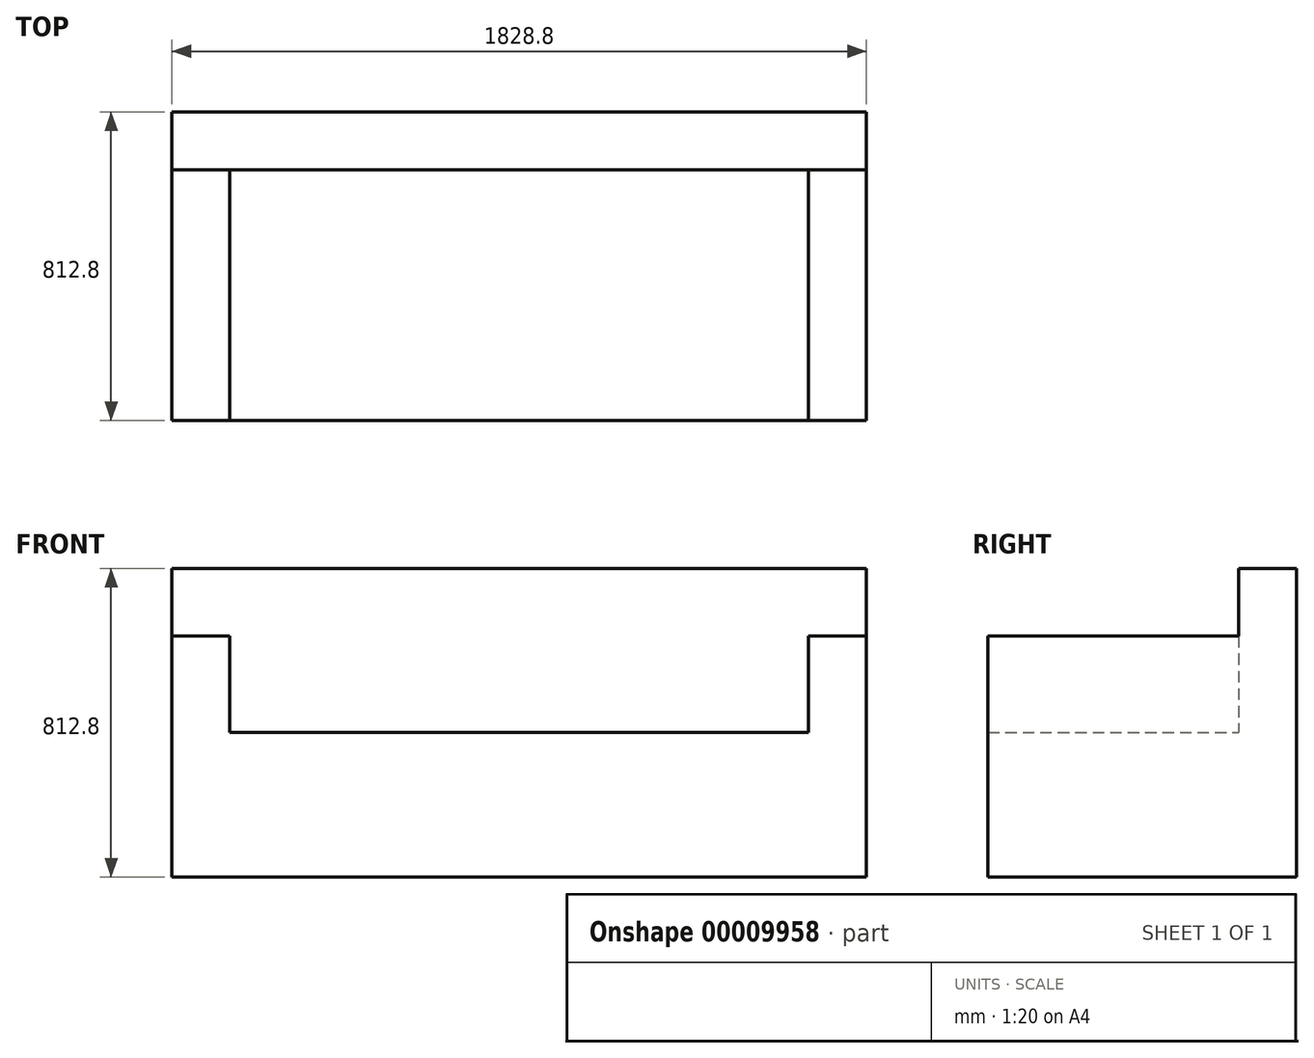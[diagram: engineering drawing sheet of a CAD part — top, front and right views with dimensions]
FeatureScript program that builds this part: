
annotation { "Feature Type Name" : "Feature", "Feature Type Description" : "" }
export const myFeature = defineFeature(function(context is Context, id is Id, definition is map)
    precondition{}
    {
        {
            var Q0;
            Q0=qCreatedBy(makeId("Top.planeOp"),FACE);
            var sketch = newSketch(context, id + "F0", { "sketchPlane" : qUnion([Q0])});
            skLineSegment(sketch, "E0.bottom", {"start": v(0, 0) * mm, "end": v(1828.8, 0) * mm});
            skLineSegment(sketch, "E0.top", {"start": v(0, -812.8) * mm, "end": v(1828.8, -812.8) * mm});
            skLineSegment(sketch, "E0.left", {"start": v(0, 0) * mm, "end": v(0, -812.8) * mm});
            skLineSegment(sketch, "E0.right", {"start": v(1828.8, 0) * mm, "end": v(1828.8, -812.8) * mm});
            skSolve(sketch);
        }
        {
            var Q0;
            Q0 = qSketchRegion(id + "F0", true);
            extrude(context, id + "F1", {"entities" : qUnion([Q0]), "depth" : 381 * mm});
        }
        {
            var Q0;
            Q0=makeQuery(id+"F1.opExtrude","CAP_FACE",FACE,{"disambiguationData":[OSD([sQuery(id+"F0.wireOp",EDGE,"E0.bottom"),sQuery(id+"F0.wireOp",EDGE,"E0.top"),sQuery(id+"F0.wireOp",EDGE,"E0.left"),sQuery(id+"F0.wireOp",EDGE,"E0.right")])],"isStart":false});
            var sketch = newSketch(context, id + "F2", { "sketchPlane" : qUnion([Q0])});
            skLineSegment(sketch, "E1", {"start": v(0, -812.8) * mm, "end": v(0, 0) * mm});
            skLineSegment(sketch, "E2", {"start": v(0, 0) * mm, "end": v(1828.8, 0) * mm});
            skLineSegment(sketch, "E3", {"start": v(1828.8, 0) * mm, "end": v(1828.8, -812.8) * mm});
            skLineSegment(sketch, "E4", {"start": v(1828.8, -812.8) * mm, "end": v(1676.4, -812.8) * mm});
            skLineSegment(sketch, "E5", {"start": v(1676.4, -812.8) * mm, "end": v(1676.4, -152.4) * mm});
            skLineSegment(sketch, "E6", {"start": v(1676.4, -152.4) * mm, "end": v(152.4, -152.4) * mm});
            skLineSegment(sketch, "E7", {"start": v(152.4, -152.4) * mm, "end": v(152.4, -812.8) * mm});
            skLineSegment(sketch, "E8", {"start": v(152.4, -812.8) * mm, "end": v(0, -812.8) * mm});
            skSolve(sketch);
        }
        {
            var Q0;
            Q0 = qSketchRegion(id + "F2", true);
            extrude(context, id + "F3", {"entities" : qUnion([Q0]), "operationType" : NewBodyOperationType.ADD, "depth" : 254 * mm});
        }
        {
            var Q0;
            Q0=makeQuery(id+"F3.opExtrude","CAP_FACE",FACE,{"disambiguationData":[OSD([sQuery(id+"F2.wireOp",EDGE,"E1"),sQuery(id+"F2.wireOp",EDGE,"E2"),sQuery(id+"F2.wireOp",EDGE,"E3"),sQuery(id+"F2.wireOp",EDGE,"E4"),sQuery(id+"F2.wireOp",EDGE,"E5"),sQuery(id+"F2.wireOp",EDGE,"E6"),sQuery(id+"F2.wireOp",EDGE,"E7"),sQuery(id+"F2.wireOp",EDGE,"E8")])],"isStart":false});
            var sketch = newSketch(context, id + "F4", { "sketchPlane" : qUnion([Q0])});
            skLineSegment(sketch, "E9.bottom", {"start": v(0, 0) * mm, "end": v(1828.8, 0) * mm});
            skLineSegment(sketch, "E9.top", {"start": v(0, -152.4) * mm, "end": v(1828.8, -152.4) * mm});
            skLineSegment(sketch, "E9.left", {"start": v(0, 0) * mm, "end": v(0, -152.4) * mm});
            skLineSegment(sketch, "E9.right", {"start": v(1828.8, 0) * mm, "end": v(1828.8, -152.4) * mm});
            skSolve(sketch);
        }
        {
            var Q0;
            Q0 = qSketchRegion(id + "F4", true);
            extrude(context, id + "F5", {"entities" : qUnion([Q0]), "operationType" : NewBodyOperationType.ADD, "depth" : 177.8 * mm});
        }
    });
